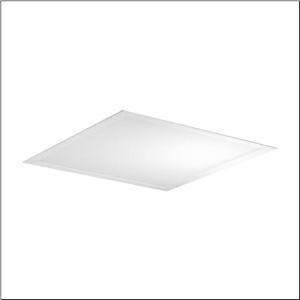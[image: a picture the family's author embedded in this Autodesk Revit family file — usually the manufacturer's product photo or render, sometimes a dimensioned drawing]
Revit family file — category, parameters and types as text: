
# Revit family: apollon_r__31_square_51mp11w72442_ea88
name_source: partatom
category: Lighting Fixtures
units: mm (PartAtom-declared; Revit-internal decimal feet)

## family parameters
Cut with Voids When Loaded = No
Host = Face
Light Source = No
Part Type = Normal
Room Calculation Point = No
Round Connector Dimension = Use Diameter
Shared = No

## types (1)
- Apollon® 31 square (1 x LED, 4000 lm, 27.5 W, 4000K)
    Apparent Load = 28 VA
    CIE Flux Codes = 61 87 97 100 100
    Color Rendering = 80
    Color Temperature = 4000K
    Default Elevation = 1800 mm
    Description = Apollon® 31 square, office luminaire, primary optical cover: micro prismatic cover, of PMMA, CAT 2 (L<= 3000cd/m²), light emission: direct distribution, primary light characteristic: symmetric, installation type: lay-in mounting, LED, rated luminous flux: 4.000lm, luminous efficacy: 145lm/W, light colour: 840, colour temperature: 4000K, with terminal, 3-pole, mains connection: 220..240V, AC, 50/60Hz, rated input power: 28W, housing, of aluminium, traffic white (RAL 9016), module: M625, length: 620mm, width: 620mm, height: 32mm, housing upper side, of sheet steel, galvanised, protection rating (complete): IP20, protection rating (on room side): IP40, insulation class (complete): insulation class II (safety insulation), certification: CE, ENEC, impact resistance: IK03, permissible operating ambient temperature: -20..+40°C, permissible storage temperature: -20..+60°C, packaging unit: 1 piece
    Height = 0 mm  [stored 0 ft]
    Lamp = 1 x LED
    Lamp Light Flux = 4000 lm
    Lamp Power = 27.5 W
    Lamp count = 1
    Length = 620 mm
    Luminous efficacy = 145 lm/W
    Manufacturer = Siteco
    ModVariant = No
    Model = 51MP11W72442
    Mounting Place = Ceiling
    Mounting Type = Recessed
    Number of Poles = 1
    OnlyDefault = Yes
    Power Factor = 1
    Product Name = Apollon® 31 square
    Product group = office luminaire | ceiling recessed
    ProductGroupID = 400
    Protection Class = Protection class II
    Protection Degree = IP 20
    RLX_Detail_Level = 1
    RLX_Emergency_Light_Flux = 0 lm
    RLX_Emergency_Type = 0
    RLX_Emergency_Type_DB = No
    RlxData = <blob elided: 12937 chars, md5=f5719baf>
    Socket = socket
    Standby Power = 0 W
    System Light Flux = 4000 lm
    System Power = 28 W
    Type Comments = Product without accessories
    Type Image = l_1291039.jpg
    URL = http://relux.com
    VarID = ---
    Voltage = 0 V
    Weight = 0.00 kg
    Width = 620 mm

note: [stored X ft] marks values corroborated as IEEE doubles in the binary element streams (Revit-internal decimal feet)

## geometry (parser evidence)
native form markers: Sweep x10
no freeform markers — native parametric forms only
